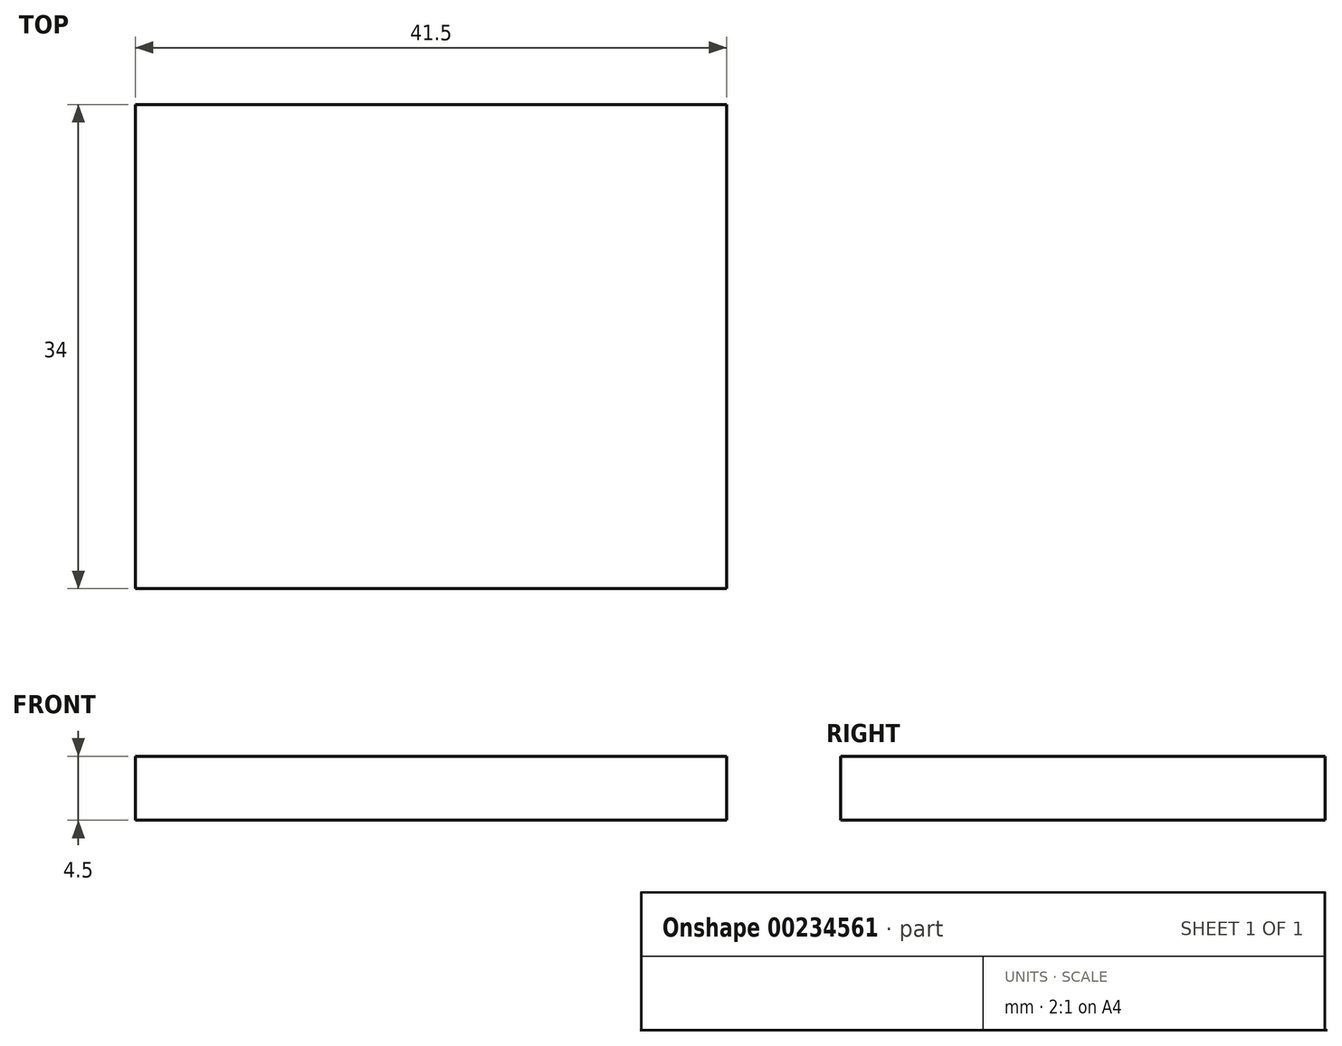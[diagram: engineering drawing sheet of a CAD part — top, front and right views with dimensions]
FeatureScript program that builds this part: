
annotation { "Feature Type Name" : "Feature", "Feature Type Description" : "" }
export const myFeature = defineFeature(function(context is Context, id is Id, definition is map)
    precondition{}
    {
        {
            var Q0;
            Q0=qCreatedBy(makeId("Top.planeOp"),FACE);
            var sketch = newSketch(context, id + "F0", { "sketchPlane" : qUnion([Q0])});
            skLineSegment(sketch, "E0.bottom", {"start": v(-20.75, 17) * mm, "end": v(20.75, 17) * mm});
            skLineSegment(sketch, "E0.top", {"start": v(-20.75, -17) * mm, "end": v(20.75, -17) * mm});
            skLineSegment(sketch, "E0.left", {"start": v(-20.75, 17) * mm, "end": v(-20.75, -17) * mm});
            skLineSegment(sketch, "E0.right", {"start": v(20.75, 17) * mm, "end": v(20.75, -17) * mm});
            skPoint(sketch, "E0.middle", {"position": v(0, 0) * mm});
            skSolve(sketch);
        }
        {
            var Q0;
            Q0=makeQuery(id+"F0.imprint","IMPRINT",FACE,{"disambiguationData":[TD([[makeQuery(id+"F0.imprint","IMPRINT",EDGE,{"derivedFrom":sQuery(id+"F0.wireOp",EDGE,"E0.bottom")}),-1.0]])]});
            extrude(context, id + "F1", {"entities" : qUnion([Q0]), "depth" : 4.5 * mm});
        }
    });
